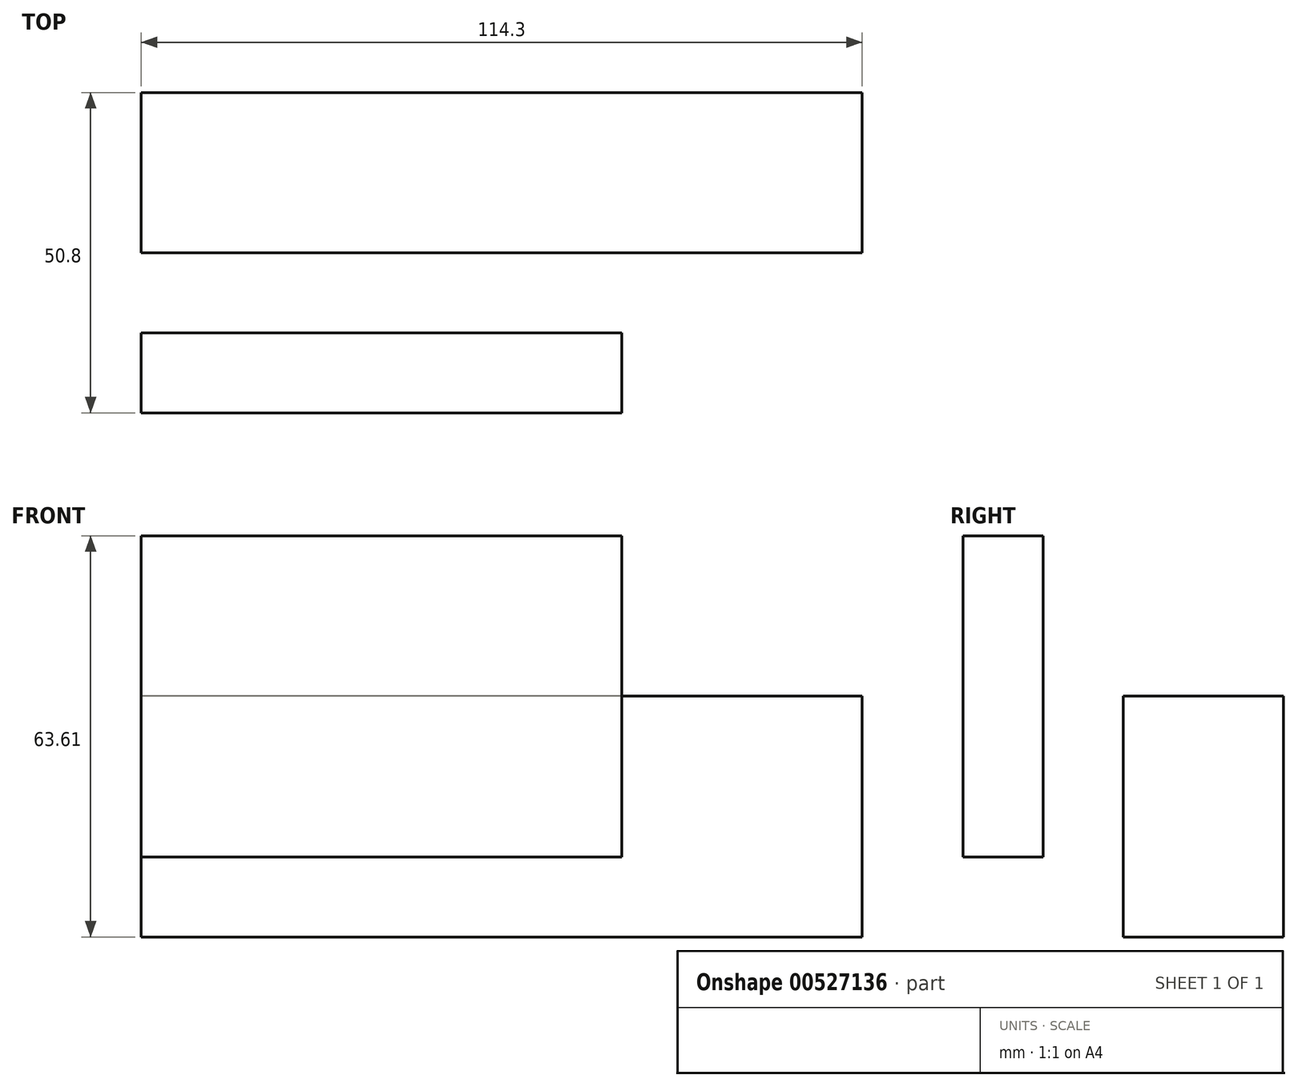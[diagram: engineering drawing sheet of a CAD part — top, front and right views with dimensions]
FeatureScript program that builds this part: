
annotation { "Feature Type Name" : "Feature", "Feature Type Description" : "" }
export const myFeature = defineFeature(function(context is Context, id is Id, definition is map)
    precondition{}
    {
        {
            var Q0;
            Q0=qCreatedBy(makeId("Right.planeOp"),FACE);
            var sketch = newSketch(context, id + "F0", { "sketchPlane" : qUnion([Q0])});
            skLineSegment(sketch, "E0.bottom", {"start": v(-28.04, 21.9) * mm, "end": v(22.76, 21.9) * mm});
            skLineSegment(sketch, "E0.top", {"start": v(-28.04, -41.7) * mm, "end": v(22.76, -41.7) * mm});
            skLineSegment(sketch, "E1.bottom", {"start": v(-28.04, 21.9) * mm, "end": v(-15.34, 21.9) * mm});
            skLineSegment(sketch, "E1.top", {"start": v(-28.04, -29) * mm, "end": v(-15.34, -29) * mm});
            skLineSegment(sketch, "E1.left", {"start": v(-28.04, 21.9) * mm, "end": v(-28.04, -29) * mm});
            skLineSegment(sketch, "E2.bottom", {"start": v(-2.64, -3.5) * mm, "end": v(22.76, -3.5) * mm});
            skLineSegment(sketch, "E2.top", {"start": v(-2.64, -41.7) * mm, "end": v(22.76, -41.7) * mm});
            skLineSegment(sketch, "E2.left", {"start": v(-2.64, -3.5) * mm, "end": v(-2.64, -41.7) * mm});
            skLineSegment(sketch, "E2.right", {"start": v(22.76, -3.5) * mm, "end": v(22.76, -41.7) * mm});
            skLineSegment(sketch, "E3", {"start": v(22.76, 21.9) * mm, "end": v(22.76, -3.5) * mm});
            skLineSegment(sketch, "E4", {"start": v(-28.04, -29) * mm, "end": v(-28.04, -41.7) * mm});
            skLineSegment(sketch, "E5", {"start": v(-15.34, -16.3) * mm, "end": v(-2.64, -16.3) * mm});
            skLineSegment(sketch, "E6", {"start": v(-15.34, -29) * mm, "end": v(-15.34, -16.3) * mm});
            skLineSegment(sketch, "E7", {"start": v(-15.34, -16.3) * mm, "end": v(-15.34, 21.9) * mm});
            skSolve(sketch);
        }
        {
            var Q0;
            Q0=makeQuery(id+"F0.imprint","IMPRINT",FACE,{"disambiguationData":[TD([[makeQuery(id+"F0.imprint","IMPRINT",EDGE,{"derivedFrom":sQuery(id+"F0.wireOp",EDGE,"E0.bottom")}),-1.0]])]});
            var Q1;
            {var subQ1=sQuery(id+"F0.wireOp",EDGE,"E0.top");Q1=makeQuery(id+"F0.imprint","IMPRINT",FACE,{"disambiguationData":[TD([[makeQuery(id+"F0.imprint","IMPRINT",EDGE,{"derivedFrom":subQ1}),1.0]])]});}
            extrude(context, id + "F1", {"entities" : qUnion([Q0, Q1]), "depth" : 76.2 * mm});
        }
        {
            var Q0;
            Q0=makeQuery(id+"F1.opExtrude","CAP_FACE",FACE,{"disambiguationData":[OSD([sQuery(id+"F0.wireOp",EDGE,"E0.bottom"),sQuery(id+"F0.wireOp",EDGE,"E0.top"),sQuery(id+"F0.wireOp",EDGE,"E1.top"),sQuery(id+"F0.wireOp",EDGE,"E2.bottom"),sQuery(id+"F0.wireOp",EDGE,"E2.left"),sQuery(id+"F0.wireOp",EDGE,"E3"),sQuery(id+"F0.wireOp",EDGE,"E4"),sQuery(id+"F0.wireOp",EDGE,"E6"),sQuery(id+"F0.wireOp",EDGE,"E7")])],"isStart":true});
            extrude(context, id + "F2", {"entities" : qUnion([Q0]), "operationType" : NewBodyOperationType.ADD, "oppositeDirection" : true, "depth" : 46.74 * mm});
        }
        {
            var Q0;
            {var subQ1=sQuery(id+"F0.wireOp",EDGE,"E0.top");Q0=makeQuery(id+"F0.imprint","IMPRINT",FACE,{"disambiguationData":[TD([[makeQuery(id+"F0.imprint","IMPRINT",EDGE,{"derivedFrom":subQ1}),1.0]])]});}
            extrude(context, id + "F3", {"entities" : qUnion([Q0]), "operationType" : NewBodyOperationType.ADD, "depth" : 114.3 * mm});
        }
    });
